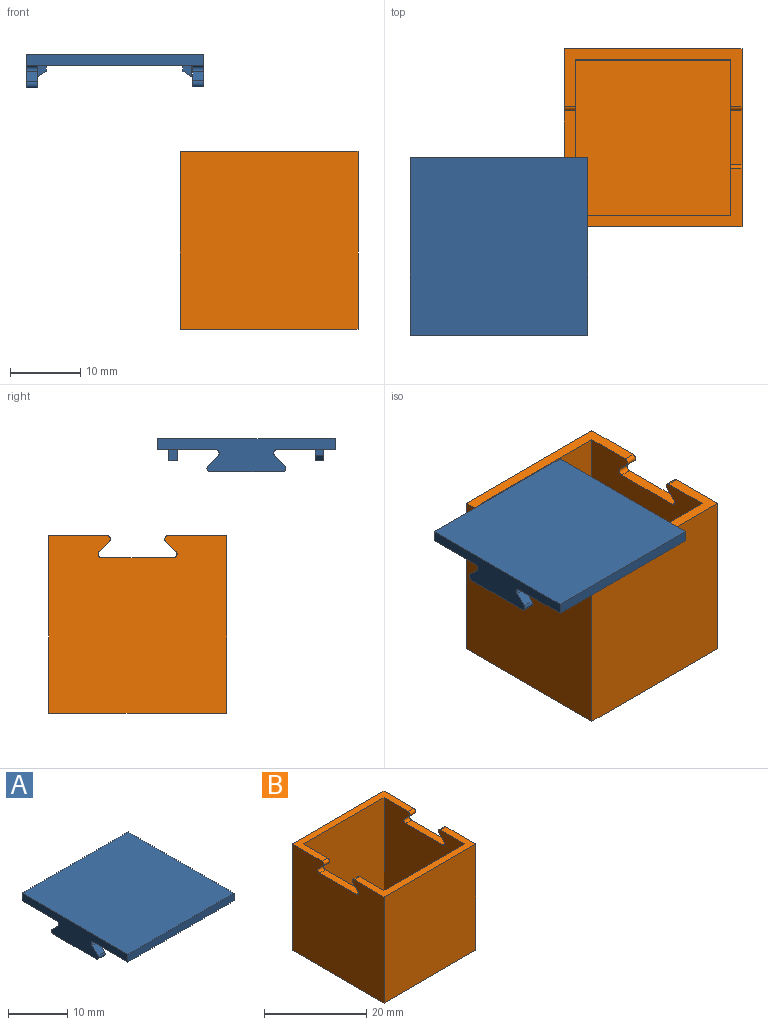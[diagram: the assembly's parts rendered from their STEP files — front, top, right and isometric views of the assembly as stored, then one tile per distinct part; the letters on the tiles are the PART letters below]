
ASSEMBLY  parts=2 mates=3
PART A: 32 faces, bbox 25.4x25.4x4.8 mm
  f0: plane 25.4x25.4mm, normal (0,0,-1), area 615.3mm2, adj f1,f2,f3,f4,f6,f7,f8,f9
  f1: plane 25.4x1.59mm, normal (0,1,0), area 40.3mm2, adj f0,f2,f4,f5
  f2: plane 25.4x4.76mm, normal (-1,0,0), area 70.6mm2, adj f0,f1,f3,f5,f16,f17,f18,f26
  f3: plane 25.4x1.59mm, normal (0,-1,0), area 40.3mm2, adj f0,f2,f4,f5
  f4: plane 25.4x4.6mm, normal (1,0,0), area 66.7mm2, adj f0,f1,f3,f5,f20,f21,f22,f24
  f5: plane 25.4x25.4mm, normal (0,0,1), area 645.2mm2, adj f1,f2,f3,f4
  f6: plane 1.59x1.27mm, normal (-1,0,0), area 2mm2, adj f0,f7,f9,f15
  f7: plane 1.59x1.27mm, normal (0,1,0), area 1.5mm2, adj f0,f6,f8,f15
  f8: plane 1.27x0.79mm, normal (1,0,0), area 1mm2, adj f0,f7,f9,f15
  f9: plane 1.59x1.27mm, normal (0,-1,0), area 1.5mm2, adj f0,f6,f8,f15
  f10: plane 1.16x0.79mm, normal (-1,0,0), area 0.9mm2, adj f0,f11,f13,f14
  f11: plane 1.59x1.27mm, normal (0,1,0), area 1.5mm2, adj f0,f10,f12,f14
  f12: plane 1.59x1.16mm, normal (1,0,0), area 1.8mm2, adj f0,f11,f13,f14
  f13: plane 1.59x1.27mm, normal (0,-1,0), area 1.5mm2, adj f0,f10,f12,f14
  f14: plane 1.27x1.16mm, normal (-0.53,0,-0.85), area 1.7mm2, adj f10,f11,f12,f13
  f15: plane 1.27x1.27mm, normal (0.53,0,-0.85), area 1.9mm2, adj f6,f7,f8,f9
  f16: plane 10.25x1.59mm, normal (0,0,-1), area 16.3mm2, adj f2,f19,f26,f27
  f17: plane 1.59x1.44mm, normal (0,-0.71,0.71), area 3.2mm2, adj f2,f19,f26,f31
  f18: plane 1.59x1.44mm, normal (0,0.71,0.71), area 3.2mm2, adj f2,f19,f27,f29
  f19: plane 11.26x3.18mm, normal (1,0,0), area 30.2mm2, adj f0,f16,f17,f18,f26,f27,f29,f31
  f20: plane 9.43x1.59mm, normal (0,0,-1), area 15mm2, adj f4,f23,f24,f25
  f21: plane 1.59x1.38mm, normal (0,0.67,0.74), area 3mm2, adj f4,f23,f24,f28
  f22: plane 1.59x1.38mm, normal (0,-0.67,0.74), area 3mm2, adj f4,f23,f25,f30
  f23: plane 10.44x3.02mm, normal (-1,0,0), area 26.3mm2, adj f0,f20,f21,f22,f24,f25,f28,f30
  f24: cylinder r=0.51mm len=1.59mm, axis (1,0,0), area 1.9mm2, adj f4,f20,f21,f23
  f25: cylinder r=0.51mm len=1.59mm, axis (1,0,0), area 1.9mm2, adj f4,f20,f22,f23
  f26: cylinder r=0.51mm len=1.59mm, axis (-1,0,0), area 1.9mm2, adj f2,f16,f17,f19
  f27: cylinder r=0.51mm len=1.59mm, axis (-1,0,0), area 1.9mm2, adj f2,f16,f18,f19
  f28: cylinder r=0.51mm len=1.59mm, axis (1,0,0), area 1.9mm2, adj f0,f4,f21,f23
  f29: cylinder r=0.51mm len=1.59mm, axis (-1,0,0), area 1.9mm2, adj f0,f2,f18,f19
  f30: cylinder r=0.51mm len=1.59mm, axis (1,0,0), area 1.9mm2, adj f0,f4,f22,f23
  f31: cylinder r=0.51mm len=1.59mm, axis (-1,0,0), area 1.9mm2, adj f0,f2,f17,f19
PART B: 26 faces, bbox 25.4x25.4x25.4 mm
  f0: plane 22.23x22.23mm, normal (0,0,1), area 494mm2, adj f1,f2,f10,f17
  f1: plane 23.81x22.23mm, normal (0,1,0), area 529.2mm2, adj f0,f8,f10,f17
  f2: plane 23.81x22.23mm, normal (0,-1,0), area 529.2mm2, adj f0,f9,f10,f17
  f3: plane 25.4x25.4mm, normal (-1,0,0), area 614.9mm2, adj f4,f6,f7,f8,f9,f14,f15,f16
  f4: plane 25.4x25.4mm, normal (0,-1,0), area 645.2mm2, adj f3,f5,f7,f8
  f5: plane 25.4x25.4mm, normal (1,0,0), area 614.9mm2, adj f4,f6,f7,f8,f9,f11,f12,f13
  f6: plane 25.4x25.4mm, normal (0,1,0), area 645.2mm2, adj f3,f5,f7,f9
  f7: plane 25.4x25.4mm, normal (0,0,-1), area 645.2mm2, adj f3,f4,f5,f6
  f8: plane 25.4x8.3mm, normal (0,0,1), area 61.6mm2, adj f1,f3,f4,f5,f10,f17,f23,f24
  f9: plane 25.4x8.3mm, normal (0,0,1), area 61.6mm2, adj f2,f3,f5,f6,f10,f17,f22,f25
  f10: plane 23.81x22.23mm, normal (-1,0,0), area 499mm2, adj f0,f1,f2,f8,f9,f11,f12,f13
  f11: plane 1.59x1.44mm, normal (0,-0.71,-0.71), area 3.2mm2, adj f5,f10,f21,f22
  f12: plane 10.25x1.59mm, normal (0,0,1), area 16.3mm2, adj f5,f10,f20,f21
  f13: plane 1.59x1.44mm, normal (0,0.71,-0.71), area 3.2mm2, adj f5,f10,f20,f23
  f14: plane 1.59x1.44mm, normal (0,0.71,-0.71), area 3.2mm2, adj f3,f17,f19,f24
  f15: plane 10.25x1.59mm, normal (0,0,1), area 16.3mm2, adj f3,f17,f18,f19
  f16: plane 1.59x1.44mm, normal (0,-0.71,-0.71), area 3.2mm2, adj f3,f17,f18,f25
  f17: plane 23.81x22.23mm, normal (1,0,0), area 499mm2, adj f0,f1,f2,f8,f9,f14,f15,f16
  f18: cylinder r=0.51mm len=1.59mm, axis (1,0,0), area 1.9mm2, adj f3,f15,f16,f17
  f19: cylinder r=0.51mm len=1.59mm, axis (1,0,0), area 1.9mm2, adj f3,f14,f15,f17
  f20: cylinder r=0.51mm len=1.59mm, axis (-1,0,0), area 1.9mm2, adj f5,f10,f12,f13
  f21: cylinder r=0.51mm len=1.59mm, axis (-1,0,0), area 1.9mm2, adj f5,f10,f11,f12
  f22: cylinder r=0.51mm len=1.59mm, axis (1,0,0), area 1.9mm2, adj f5,f9,f10,f11
  f23: cylinder r=0.51mm len=1.59mm, axis (1,0,0), area 1.9mm2, adj f5,f8,f10,f13
  f24: cylinder r=0.51mm len=1.59mm, axis (-1,0,0), area 1.9mm2, adj f3,f8,f14,f17
  f25: cylinder r=0.51mm len=1.59mm, axis (-1,0,0), area 1.9mm2, adj f3,f9,f16,f17
PLACE A t=(-45.74,-36.08,-9.94)mm
PLACE B t=(-24.78,-15.38,-47.58)mm
MATE parallel A.f4 <-> B.f5  axis (1,0,0) through (-28.52,-38.47,-10.1)mm
MATE parallel A.f3 <-> B.f4  axis (0,-1,0) through (-41.22,-51.17,-9.15)mm
MATE parallel A.f1 <-> B.f6  axis (0,1,0) through (-28.52,-25.77,-8.35)mm
